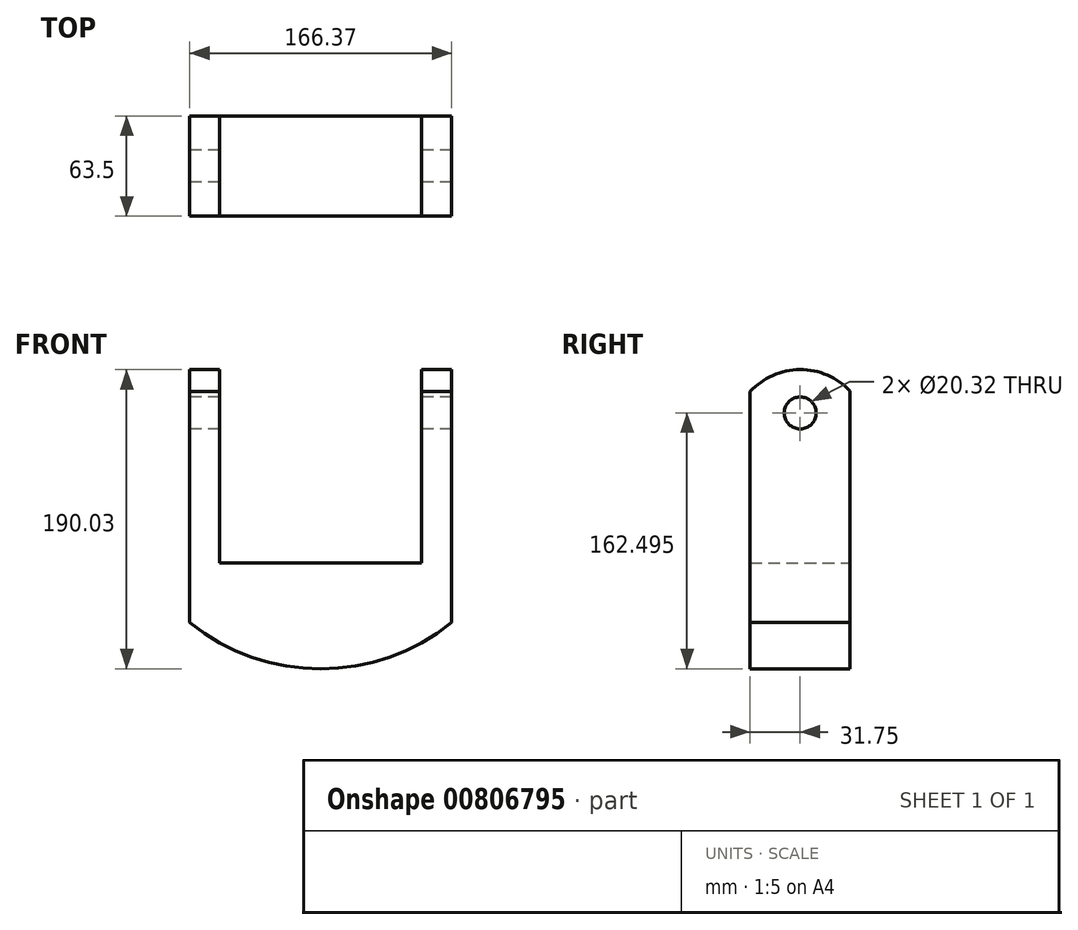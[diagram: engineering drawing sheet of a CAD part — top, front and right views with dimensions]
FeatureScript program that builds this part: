
annotation { "Feature Type Name" : "Feature", "Feature Type Description" : "" }
export const myFeature = defineFeature(function(context is Context, id is Id, definition is map)
    precondition{}
    {
        {
            var Q0;
            Q0=qCreatedBy(makeId("Front.planeOp"),FACE);
            var sketch = newSketch(context, id + "F0", { "sketchPlane" : qUnion([Q0])});
            skLineSegment(sketch, "E0", {"start": v(-108.2, -75.37) * mm, "end": v(58.16, -75.37) * mm});
            skLineSegment(sketch, "E1", {"start": v(58.16, -75.37) * mm, "end": v(58.16, 92.4) * mm});
            skLineSegment(sketch, "E2", {"start": v(58.16, 92.4) * mm, "end": v(39.11, 92.4) * mm});
            skLineSegment(sketch, "E3", {"start": v(39.11, 92.4) * mm, "end": v(39.11, -37.71) * mm});
            skLineSegment(sketch, "E4", {"start": v(39.11, -37.71) * mm, "end": v(-89.16, -37.71) * mm});
            skLineSegment(sketch, "E5", {"start": v(-89.16, -37.71) * mm, "end": v(-89.16, 89.46) * mm});
            skLineSegment(sketch, "E6", {"start": v(-89.16, 89.46) * mm, "end": v(-108.2, 89.46) * mm});
            skLineSegment(sketch, "E7", {"start": v(-108.2, 89.46) * mm, "end": v(-108.2, -75.37) * mm});
            skArc(sketch, "E8", {"start": v(-108.2, -75.37) * mm, "mid": v(-25.02, -104.8) * mm, "end": v(58.16, -75.37) * mm});
            skSolve(sketch);
        }
        {
            var Q0;
            Q0=makeQuery(id+"F0.imprint","IMPRINT",FACE,{"disambiguationData":[TD([[makeQuery(id+"F0.imprint","IMPRINT",EDGE,{"derivedFrom":sQuery(id+"F0.wireOp",EDGE,"E0")}),1.0]])]});
            var Q1;
            Q1=makeQuery(id+"F0.imprint","IMPRINT",FACE,{"disambiguationData":[TD([[makeQuery(id+"F0.imprint","IMPRINT",EDGE,{"derivedFrom":sQuery(id+"F0.wireOp",EDGE,"E0")}),-1.0]])]});
            extrude(context, id + "F1", {"entities" : qUnion([Q0, Q1]), "endBound" : BoundingType.SYMMETRIC, "depth" : 63.5 * mm, "offsetDistance" : 25.4 * mm});
        }
        {
            var Q0;
            Q0=makeQuery(id+"F1.opExtrude","SWEPT_FACE",FACE,{"disambiguationData":[OSD([sQuery(id+"F0.wireOp",EDGE,"E7")])]});
            var sketch = newSketch(context, id + "F2", { "sketchPlane" : qUnion([Q0])});
            skPoint(sketch, "E9", {"position": v(0, 57.7) * mm});
            skPoint(sketch, "E9.positionSnap0", {"position": v(0, 89.46) * mm});
            skCircle(sketch, "E10", {"center": v(0, 57.7) * mm, "radius": 10.16 * mm});
            skSolve(sketch);
        }
        {
            var Q0;
            Q0=makeQuery(id+"F2.imprint","IMPRINT",FACE,{"disambiguationData":[TD([[makeQuery(id+"F2.imprint","IMPRINT",EDGE,{"derivedFrom":sQuery(id+"F2.wireOp",EDGE,"E10")}),1.0]])]});
            var Q1;
            Q1=sQuery(id+"F2.wireOp",EDGE,"E10");
            extrude(context, id + "F3", {"entities" : qUnion([Q0]), "operationType" : NewBodyOperationType.REMOVE, "surfaceEntities" : qUnion([Q1]), "endBound" : BoundingType.THROUGH_ALL, "oppositeDirection" : true, "depth" : 25.4 * mm, "offsetDistance" : 25.4 * mm});
        }
        {
            var Q0;
            Q0=makeQuery(id+"F1.opExtrude","SWEPT_FACE",FACE,{"disambiguationData":[OSD([sQuery(id+"F0.wireOp",EDGE,"E1")])]});
            var sketch = newSketch(context, id + "F4", { "sketchPlane" : qUnion([Q0])});
            skArc(sketch, "E11", {"start": v(31.75, 71.64) * mm, "mid": v(-0.08, 85.24) * mm, "end": v(-31.75, 71.28) * mm});
            skSolve(sketch);
        }
        {
            var Q0;
            {var subQ0=sQuery(id+"F4.wireOp",EDGE,"E11");Q0=makeQuery(id+"F4.imprint","IMPRINT",FACE,{"disambiguationData":[TD([[makeQuery(id+"F4.imprint","IMPRINT",EDGE,{"derivedFrom":subQ0}),-1.0]])]});}
            extrude(context, id + "F5", {"entities" : qUnion([Q0]), "operationType" : NewBodyOperationType.REMOVE, "endBound" : BoundingType.THROUGH_ALL, "oppositeDirection" : true, "depth" : 25.4 * mm, "offsetDistance" : 25.4 * mm});
        }
    });
